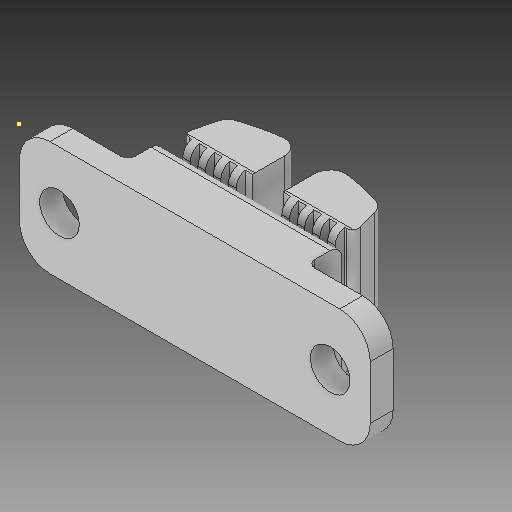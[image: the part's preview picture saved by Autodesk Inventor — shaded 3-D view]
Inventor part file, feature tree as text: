
AUTODESK INVENTOR PART (.ipt)
format: ipt  version: 2017 (Build 210142000, 142)  size: 275,456 bytes
history: native  units: mm
features: sketch x12, other x3
ambient origin geometry x8: Origin, YZ Plane, XZ Plane, XY Plane, X Axis, Y Axis, Z Axis, Center Point
bodies: Solid1 (feature_tree)
feature tree (15):
  other  "X Belt Clamp.ipt"
  other  "Solid1::X Belt Clamp.ipt"
  other  "TaggingFeature1"
  sketch  "Sketch1"  dims[d0=10.0mm]
  sketch  "Sketch2"
  sketch  "Sketch3"
  sketch  "Sketch4"
  sketch  "Sketch5"
  sketch  "Sketch6"
  sketch  "Sketch7"
  sketch  "Sketch8"
  sketch  "Sketch9"
  sketch  "Sketch10"
  sketch  "Sketch11"
  sketch  "Sketch12"
